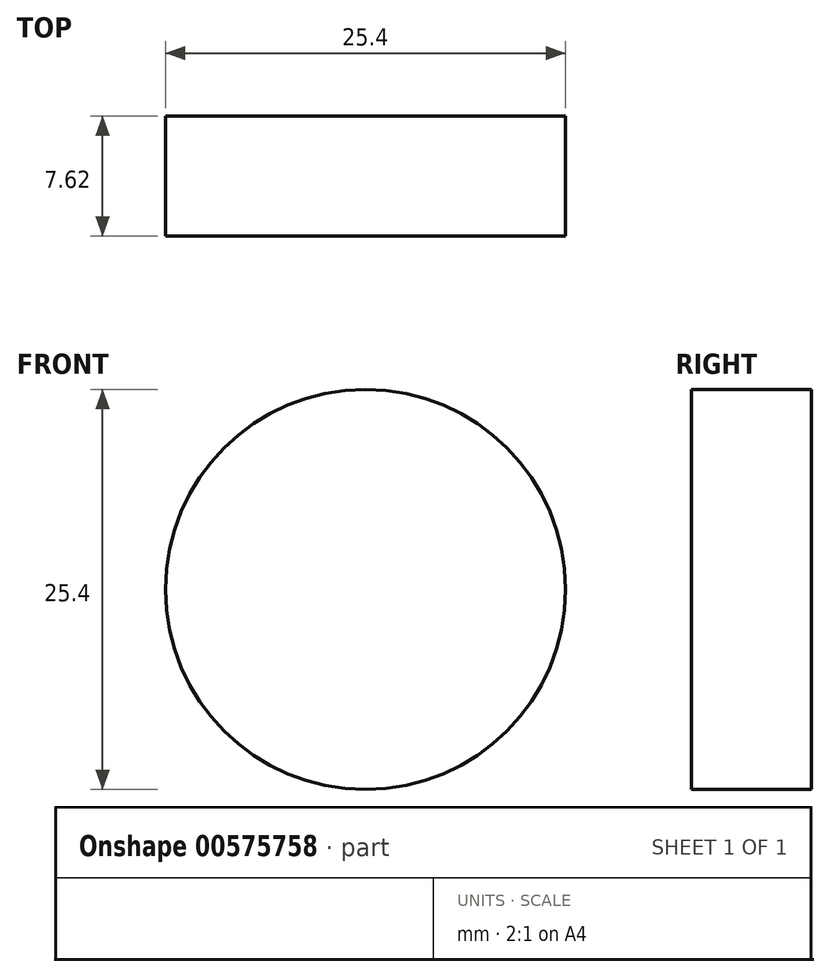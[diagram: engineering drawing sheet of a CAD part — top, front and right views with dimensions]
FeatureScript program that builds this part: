
annotation { "Feature Type Name" : "Feature", "Feature Type Description" : "" }
export const myFeature = defineFeature(function(context is Context, id is Id, definition is map)
    precondition{}
    {
        {
            var Q0;
            Q0=qCreatedBy(makeId("Front.planeOp"),FACE);
            var sketch = newSketch(context, id + "F0", { "sketchPlane" : qUnion([Q0])});
            skCircle(sketch, "E0", {"center": v(0, 0) * mm, "radius": 12.7 * mm});
            skSolve(sketch);
        }
        {
            var Q0;
            Q0 = qSketchRegion(id + "F0", true);
            var Q1;
            Q1=makeQuery(id+"F0.imprint","IMPRINT",FACE,{"disambiguationData":[TD([[makeQuery(id+"F0.imprint","IMPRINT",EDGE,{"derivedFrom":sQuery(id+"F0.wireOp",EDGE,"E0")}),1.0]])]});
            extrude(context, id + "F1", {"entities" : qUnion([Q0, Q1]), "depth" : 7.62 * mm, "offsetDistance" : 25.4 * mm});
        }
    });
